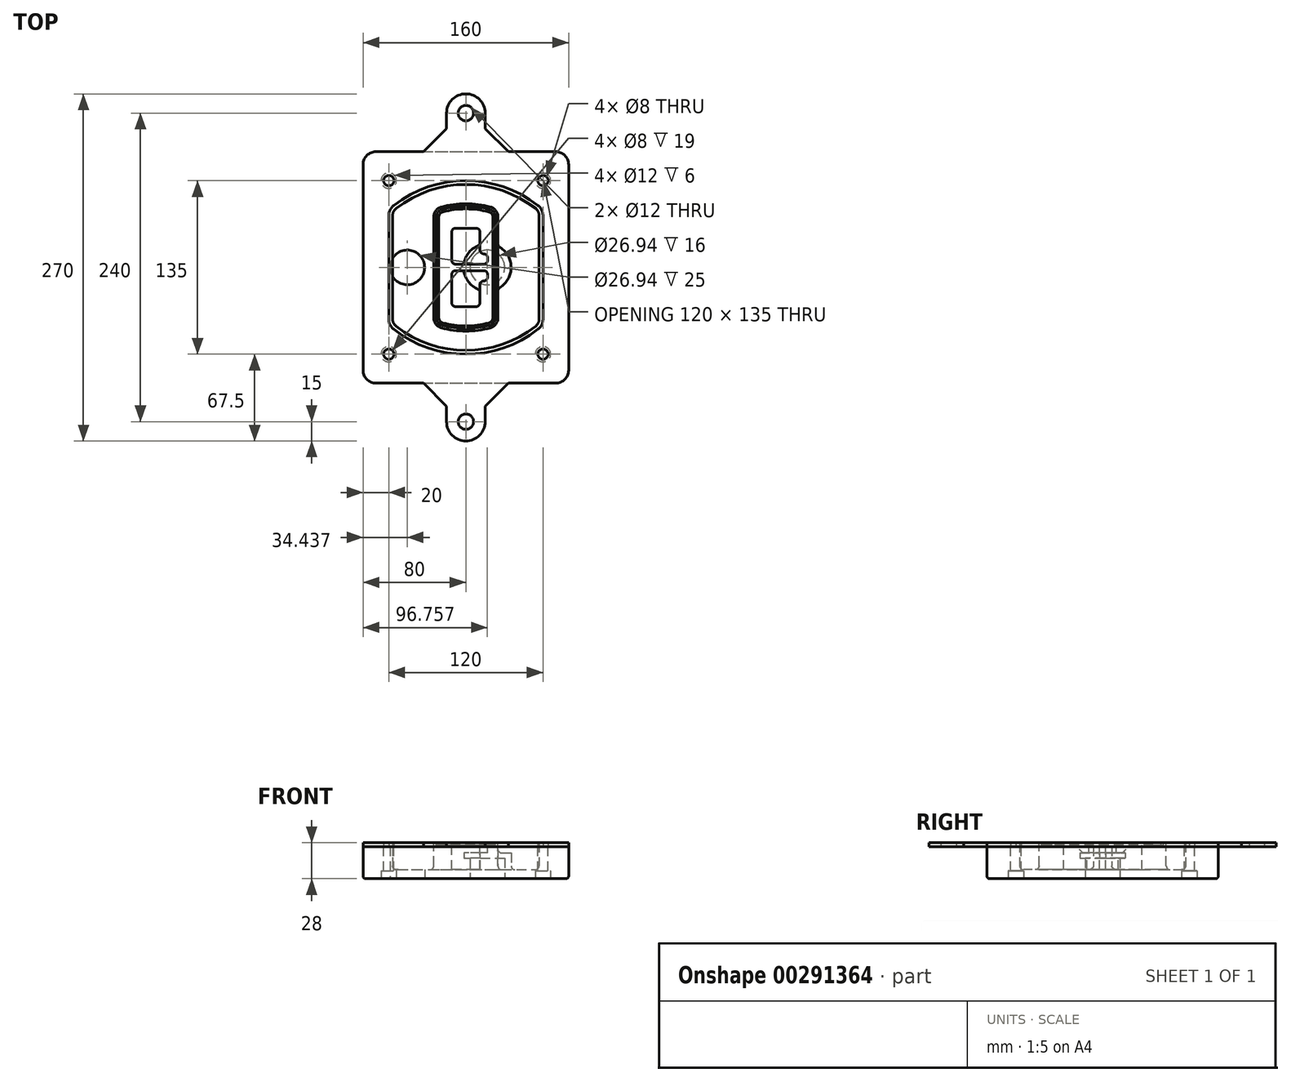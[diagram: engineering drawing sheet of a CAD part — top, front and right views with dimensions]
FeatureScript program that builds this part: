
annotation { "Feature Type Name" : "Feature", "Feature Type Description" : "" }
export const myFeature = defineFeature(function(context is Context, id is Id, definition is map)
    precondition{}
    {
        {
            var Q0;
            Q0=qCreatedBy(makeId("Top.planeOp"),FACE);
            var sketch = newSketch(context, id + "F0", { "sketchPlane" : qUnion([Q0])});
            skPoint(sketch, "E0.rect.middle", {"position": v(0, 0) * mm});
            skLineSegment(sketch, "E1.bottom", {"start": v(-70, -90) * mm, "end": v(70, -90) * mm});
            skLineSegment(sketch, "E1.top", {"start": v(-70, 90) * mm, "end": v(70, 90) * mm});
            skLineSegment(sketch, "E1.left", {"start": v(-80, -80) * mm, "end": v(-80, 80) * mm});
            skLineSegment(sketch, "E1.right", {"start": v(80, -80) * mm, "end": v(80, 80) * mm});
            skLineSegment(sketch, "E2", {"start": v(-80, 90) * mm, "end": v(80, -90) * mm, "construction": true});
            skLineSegment(sketch, "E3", {"start": v(80, 90) * mm, "end": v(-80, -90) * mm, "construction": true});
            skCircle(sketch, "E4", {"center": v(-60, 67.5) * mm, "radius": 4 * mm});
            skCircle(sketch, "E5", {"center": v(60, 67.5) * mm, "radius": 4 * mm});
            skCircle(sketch, "E6", {"center": v(60, -67.5) * mm, "radius": 4 * mm});
            skCircle(sketch, "E7", {"center": v(-60, -67.5) * mm, "radius": 4 * mm});
            skLineSegment(sketch, "E8", {"start": v(-60, 67.5) * mm, "end": v(60, 67.5) * mm, "construction": true});
            skLineSegment(sketch, "E9", {"start": v(60, 67.5) * mm, "end": v(60, -67.5) * mm, "construction": true});
            skLineSegment(sketch, "E10", {"start": v(60, -67.5) * mm, "end": v(-60, -67.5) * mm, "construction": true});
            skLineSegment(sketch, "E11", {"start": v(-60, -67.5) * mm, "end": v(-60, 67.5) * mm, "construction": true});
            skLineSegment(sketch, "E12", {"start": v(-60, 40.3) * mm, "end": v(-60, -40.3) * mm});
            skLineSegment(sketch, "E13", {"start": v(60, 40.3) * mm, "end": v(60, -40.3) * mm});
            skArc(sketch, "E14", {"start": v(56.15, 48.18) * mm, "mid": v(0, 67.5) * mm, "end": v(-56.15, 48.18) * mm});
            skArc(sketch, "E15", {"start": v(-56.15, -48.18) * mm, "mid": v(0, -67.5) * mm, "end": v(56.15, -48.18) * mm});
            skLineSegment(sketch, "E16", {"start": v(-60, 0) * mm, "end": v(60, 0) * mm, "construction": true});
            skPoint(sketch, "E17.visualSharp", {"position": v(-60, -45) * mm});
            skArc(sketch, "E17.filletArc", {"start": v(-60, -40.3) * mm, "mid": v(-58.99, -44.68) * mm, "end": v(-56.15, -48.18) * mm});
            skPoint(sketch, "E18.visualSharp", {"position": v(-60, 45) * mm});
            skArc(sketch, "E18.filletArc", {"start": v(-56.15, 48.18) * mm, "mid": v(-58.99, 44.68) * mm, "end": v(-60, 40.3) * mm});
            skPoint(sketch, "E19.visualSharp", {"position": v(60, 45) * mm});
            skArc(sketch, "E19.filletArc", {"start": v(60, 40.3) * mm, "mid": v(58.99, 44.68) * mm, "end": v(56.15, 48.18) * mm});
            skPoint(sketch, "E20.visualSharp", {"position": v(60, -45) * mm});
            skArc(sketch, "E20.filletArc", {"start": v(56.15, -48.18) * mm, "mid": v(58.99, -44.68) * mm, "end": v(60, -40.3) * mm});
            skPoint(sketch, "E21.visualSharp", {"position": v(-80, 90) * mm});
            skArc(sketch, "E21.filletArc", {"start": v(-70, 90) * mm, "mid": v(-77.07, 87.07) * mm, "end": v(-80, 80) * mm});
            skPoint(sketch, "E22.visualSharp", {"position": v(80, 90) * mm});
            skArc(sketch, "E22.filletArc", {"start": v(80, 80) * mm, "mid": v(77.07, 87.07) * mm, "end": v(70, 90) * mm});
            skPoint(sketch, "E23.visualSharp", {"position": v(80, -90) * mm});
            skArc(sketch, "E23.filletArc", {"start": v(70, -90) * mm, "mid": v(77.07, -87.07) * mm, "end": v(80, -80) * mm});
            skPoint(sketch, "E24.visualSharp", {"position": v(-80, -90) * mm});
            skArc(sketch, "E24.filletArc", {"start": v(-80, -80) * mm, "mid": v(-77.07, -87.07) * mm, "end": v(-70, -90) * mm});
            skArc(sketch, "E25.0", {"start": v(57, 40.3) * mm, "mid": v(56.3, 43.36) * mm, "end": v(54.3, 45.81) * mm});
            skLineSegment(sketch, "E25.1", {"start": v(57, 40.3) * mm, "end": v(57, -40.3) * mm});
            skArc(sketch, "E25.2", {"start": v(54.3, -45.81) * mm, "mid": v(56.3, -43.36) * mm, "end": v(57, -40.3) * mm});
            skArc(sketch, "E25.3", {"start": v(-54.3, -45.81) * mm, "mid": v(0, -64.5) * mm, "end": v(54.3, -45.81) * mm});
            skArc(sketch, "E25.4", {"start": v(-57, -40.3) * mm, "mid": v(-56.3, -43.36) * mm, "end": v(-54.3, -45.81) * mm});
            skArc(sketch, "E25.5", {"start": v(54.3, 45.81) * mm, "mid": v(0, 64.5) * mm, "end": v(-54.3, 45.81) * mm});
            skLineSegment(sketch, "E25.6", {"start": v(-57, 40.3) * mm, "end": v(-57, -40.3) * mm});
            skArc(sketch, "E25.7", {"start": v(-54.3, 45.81) * mm, "mid": v(-56.3, 43.36) * mm, "end": v(-57, 40.3) * mm});
            skArc(sketch, "E26.0", {"start": v(-58.62, 51.33) * mm, "mid": v(-62.58, 46.43) * mm, "end": v(-64, 40.3) * mm});
            skArc(sketch, "E26.1", {"start": v(58.62, 51.33) * mm, "mid": v(0, 71.5) * mm, "end": v(-58.62, 51.33) * mm});
            skArc(sketch, "E26.2", {"start": v(64, 40.3) * mm, "mid": v(62.58, 46.43) * mm, "end": v(58.62, 51.33) * mm});
            skLineSegment(sketch, "E26.3", {"start": v(64, 40.3) * mm, "end": v(64, -40.3) * mm});
            skArc(sketch, "E26.4", {"start": v(58.62, -51.33) * mm, "mid": v(62.58, -46.43) * mm, "end": v(64, -40.3) * mm});
            skLineSegment(sketch, "E26.5", {"start": v(-64, 40.3) * mm, "end": v(-64, -40.3) * mm});
            skArc(sketch, "E26.6", {"start": v(-58.62, -51.33) * mm, "mid": v(0, -71.5) * mm, "end": v(58.62, -51.33) * mm});
            skArc(sketch, "E26.7", {"start": v(-64, -40.3) * mm, "mid": v(-62.58, -46.43) * mm, "end": v(-58.62, -51.33) * mm});
            skSolve(sketch);
        }
        {
            var Q0;
            Q0=makeQuery(id+"F0.imprint","IMPRINT",FACE,{"disambiguationData":[TD([[makeQuery(id+"F0.imprint","IMPRINT",EDGE,{"derivedFrom":sQuery(id+"F0.wireOp",EDGE,"E1.bottom")}),1.0]])]});
            var Q1;
            Q1=makeQuery(id+"F0.imprint","IMPRINT",FACE,{"disambiguationData":[TD([[makeQuery(id+"F0.imprint","IMPRINT",EDGE,{"derivedFrom":sQuery(id+"F0.wireOp",EDGE,"E12")}),1.0]])]});
            var Q2;
            Q2=makeQuery(id+"F0.imprint","IMPRINT",FACE,{"disambiguationData":[TD([[makeQuery(id+"F0.imprint","IMPRINT",EDGE,{"derivedFrom":sQuery(id+"F0.wireOp",EDGE,"E25.0")}),1.0]])]});
            var Q3;
            Q3=makeQuery(id+"F0.imprint","IMPRINT",FACE,{"disambiguationData":[TD([[makeQuery(id+"F0.imprint","IMPRINT",EDGE,{"derivedFrom":sQuery(id+"F0.wireOp",EDGE,"E12")}),-1.0]])]});
            extrude(context, id + "F1", {"entities" : qUnion([Q0, Q1, Q2, Q3]), "oppositeDirection" : true, "depth" : 25 * mm});
        }
        {
            var Q0;
            Q0=makeQuery(id+"F0.imprint","IMPRINT",FACE,{"disambiguationData":[TD([[makeQuery(id+"F0.imprint","IMPRINT",EDGE,{"derivedFrom":sQuery(id+"F0.wireOp",EDGE,"E12")}),1.0]])]});
            extrude(context, id + "F2", {"entities" : qUnion([Q0]), "operationType" : NewBodyOperationType.ADD, "depth" : 3 * mm});
        }
        {
            var Q0;
            Q0=makeQuery(id+"F0.imprint","IMPRINT",FACE,{"disambiguationData":[TD([[makeQuery(id+"F0.imprint","IMPRINT",EDGE,{"derivedFrom":sQuery(id+"F0.wireOp",EDGE,"E25.0")}),1.0]])]});
            extrude(context, id + "F3", {"entities" : qUnion([Q0]), "operationType" : NewBodyOperationType.REMOVE, "oppositeDirection" : true, "depth" : 18 * mm});
        }
        {
            var Q0;
            Q0=makeQuery(id+"F2.opExtrude","CAP_FACE",FACE,{"disambiguationData":[OSD([sQuery(id+"F0.wireOp",EDGE,"E12"),sQuery(id+"F0.wireOp",EDGE,"E13"),sQuery(id+"F0.wireOp",EDGE,"E14"),sQuery(id+"F0.wireOp",EDGE,"E15"),sQuery(id+"F0.wireOp",EDGE,"E17.filletArc"),sQuery(id+"F0.wireOp",EDGE,"E18.filletArc"),sQuery(id+"F0.wireOp",EDGE,"E19.filletArc"),sQuery(id+"F0.wireOp",EDGE,"E20.filletArc"),sQuery(id+"F0.wireOp",EDGE,"E25.0"),sQuery(id+"F0.wireOp",EDGE,"E25.1"),sQuery(id+"F0.wireOp",EDGE,"E25.2"),sQuery(id+"F0.wireOp",EDGE,"E25.3"),sQuery(id+"F0.wireOp",EDGE,"E25.4"),sQuery(id+"F0.wireOp",EDGE,"E25.5"),sQuery(id+"F0.wireOp",EDGE,"E25.6"),sQuery(id+"F0.wireOp",EDGE,"E25.7")])],"isStart":false});
            var sketch = newSketch(context, id + "F4", { "sketchPlane" : qUnion([Q0])});
            skArc(sketch, "E27.0", {"start": v(-19.08, -46.97) * mm, "mid": v(0, -49.5) * mm, "end": v(19.08, -46.97) * mm});
            skArc(sketch, "E28.0", {"start": v(19.08, 46.97) * mm, "mid": v(0, 49.5) * mm, "end": v(-19.08, 46.97) * mm});
            skLineSegment(sketch, "E29", {"start": v(-25, 39.25) * mm, "end": v(-25, -39.25) * mm});
            skLineSegment(sketch, "E30", {"start": v(25, 39.25) * mm, "end": v(25, -39.25) * mm});
            skLineSegment(sketch, "E31", {"start": v(-25, 45.1) * mm, "end": v(25, 45.1) * mm, "construction": true});
            skLineSegment(sketch, "E32", {"start": v(-25, -45.1) * mm, "end": v(25, -45.1) * mm, "construction": true});
            skPoint(sketch, "E33.visualSharp", {"position": v(-25, 45.1) * mm});
            skArc(sketch, "E33.filletArc", {"start": v(-19.08, 46.97) * mm, "mid": v(-23.35, 44.11) * mm, "end": v(-25, 39.25) * mm});
            skPoint(sketch, "E34.visualSharp", {"position": v(25, 45.1) * mm});
            skArc(sketch, "E34.filletArc", {"start": v(25, 39.25) * mm, "mid": v(23.35, 44.11) * mm, "end": v(19.08, 46.97) * mm});
            skPoint(sketch, "E35.visualSharp", {"position": v(25, -45.1) * mm});
            skArc(sketch, "E35.filletArc", {"start": v(19.08, -46.97) * mm, "mid": v(23.35, -44.11) * mm, "end": v(25, -39.25) * mm});
            skPoint(sketch, "E36.visualSharp", {"position": v(-25, -45.1) * mm});
            skArc(sketch, "E36.filletArc", {"start": v(-25, -39.25) * mm, "mid": v(-23.35, -44.11) * mm, "end": v(-19.08, -46.97) * mm});
            skArc(sketch, "E37.0", {"start": v(54.3, 45.81) * mm, "mid": v(0, 64.5) * mm, "end": v(-54.3, 45.81) * mm});
            skArc(sketch, "E37.1", {"start": v(-54.3, 45.81) * mm, "mid": v(-56.3, 43.36) * mm, "end": v(-57, 40.3) * mm});
            skLineSegment(sketch, "E37.2", {"start": v(-57, 40.3) * mm, "end": v(-57, -40.3) * mm});
            skArc(sketch, "E37.3", {"start": v(-57, -40.3) * mm, "mid": v(-56.3, -43.36) * mm, "end": v(-54.3, -45.81) * mm});
            skArc(sketch, "E37.4", {"start": v(-54.3, -45.81) * mm, "mid": v(0, -64.5) * mm, "end": v(54.3, -45.81) * mm});
            skArc(sketch, "E37.5", {"start": v(54.3, -45.81) * mm, "mid": v(56.3, -43.36) * mm, "end": v(57, -40.3) * mm});
            skLineSegment(sketch, "E37.6", {"start": v(57, 40.3) * mm, "end": v(57, -40.3) * mm});
            skArc(sketch, "E37.7", {"start": v(57, 40.3) * mm, "mid": v(56.3, 43.36) * mm, "end": v(54.3, 45.81) * mm});
            skLineSegment(sketch, "E38.0", {"start": v(23, 39.25) * mm, "end": v(23, -39.25) * mm});
            skArc(sketch, "E38.1", {"start": v(18.56, -45.04) * mm, "mid": v(21.76, -42.9) * mm, "end": v(23, -39.25) * mm});
            skArc(sketch, "E38.2", {"start": v(-18.56, -45.04) * mm, "mid": v(0, -47.5) * mm, "end": v(18.56, -45.04) * mm});
            skArc(sketch, "E38.3", {"start": v(-23, -39.25) * mm, "mid": v(-21.76, -42.9) * mm, "end": v(-18.56, -45.04) * mm});
            skLineSegment(sketch, "E38.4", {"start": v(-23, 39.25) * mm, "end": v(-23, -39.25) * mm});
            skArc(sketch, "E38.5", {"start": v(23, 39.25) * mm, "mid": v(21.76, 42.9) * mm, "end": v(18.56, 45.04) * mm});
            skArc(sketch, "E38.6", {"start": v(-18.56, 45.04) * mm, "mid": v(-21.76, 42.9) * mm, "end": v(-23, 39.25) * mm});
            skArc(sketch, "E38.7", {"start": v(18.56, 45.04) * mm, "mid": v(0, 47.5) * mm, "end": v(-18.56, 45.04) * mm});
            skArc(sketch, "E39.0", {"start": v(21, 39.25) * mm, "mid": v(20.18, 41.68) * mm, "end": v(18.04, 43.1) * mm});
            skLineSegment(sketch, "E39.1", {"start": v(21, 39.25) * mm, "end": v(21, -39.25) * mm});
            skArc(sketch, "E39.2", {"start": v(18.04, -43.1) * mm, "mid": v(20.18, -41.68) * mm, "end": v(21, -39.25) * mm});
            skArc(sketch, "E39.3", {"start": v(-18.04, -43.1) * mm, "mid": v(0, -45.5) * mm, "end": v(18.04, -43.1) * mm});
            skArc(sketch, "E39.4", {"start": v(-21, -39.25) * mm, "mid": v(-20.18, -41.68) * mm, "end": v(-18.04, -43.1) * mm});
            skArc(sketch, "E39.5", {"start": v(18.04, 43.1) * mm, "mid": v(0, 45.5) * mm, "end": v(-18.04, 43.1) * mm});
            skLineSegment(sketch, "E39.6", {"start": v(-21, 39.25) * mm, "end": v(-21, -39.25) * mm});
            skArc(sketch, "E39.7", {"start": v(-18.04, 43.1) * mm, "mid": v(-20.18, 41.68) * mm, "end": v(-21, 39.25) * mm});
            skLineSegment(sketch, "E40", {"start": v(-25, 0) * mm, "end": v(25, 0) * mm, "construction": true});
            skLineSegment(sketch, "E41", {"start": v(-11, 5.5) * mm, "end": v(-11, 27.5) * mm});
            skLineSegment(sketch, "E42", {"start": v(-8, 30.5) * mm, "end": v(8, 30.5) * mm});
            skLineSegment(sketch, "E43", {"start": v(11, 27.5) * mm, "end": v(11, 13.5) * mm});
            skLineSegment(sketch, "E44", {"start": v(14, 10.5) * mm, "end": v(14, 10.5) * mm});
            skLineSegment(sketch, "E45", {"start": v(17, 7.5) * mm, "end": v(17, 5.5) * mm});
            skLineSegment(sketch, "E46", {"start": v(14, 2.5) * mm, "end": v(-8, 2.5) * mm});
            skPoint(sketch, "E47.visualSharp", {"position": v(-11, 30.5) * mm});
            skArc(sketch, "E47.filletArc", {"start": v(-8, 30.5) * mm, "mid": v(-10.12, 29.62) * mm, "end": v(-11, 27.5) * mm});
            skPoint(sketch, "E48.visualSharp", {"position": v(11, 30.5) * mm});
            skArc(sketch, "E48.filletArc", {"start": v(11, 27.5) * mm, "mid": v(10.12, 29.62) * mm, "end": v(8, 30.5) * mm});
            skPoint(sketch, "E49.visualSharp", {"position": v(11, 10.5) * mm});
            skArc(sketch, "E49.filletArc", {"start": v(11, 13.5) * mm, "mid": v(11.88, 11.38) * mm, "end": v(14, 10.5) * mm});
            skPoint(sketch, "E50.visualSharp", {"position": v(17, 10.5) * mm});
            skArc(sketch, "E50.filletArc", {"start": v(17, 7.5) * mm, "mid": v(16.12, 9.62) * mm, "end": v(14, 10.5) * mm});
            skPoint(sketch, "E51.visualSharp", {"position": v(17, 2.5) * mm});
            skArc(sketch, "E51.filletArc", {"start": v(14, 2.5) * mm, "mid": v(16.12, 3.38) * mm, "end": v(17, 5.5) * mm});
            skPoint(sketch, "E52.visualSharp", {"position": v(-11, 2.5) * mm});
            skArc(sketch, "E52.filletArc", {"start": v(-11, 5.5) * mm, "mid": v(-10.12, 3.38) * mm, "end": v(-8, 2.5) * mm});
            skLineSegment(sketch, "E53.0.MirrorCS", {"start": v(14, -2.5) * mm, "end": v(-8, -2.5) * mm});
            skArc(sketch, "E54.0.MirrorCS", {"start": v(-11, -5.5) * mm, "mid": v(-10.12, -3.38) * mm, "end": v(-8, -2.5) * mm});
            skLineSegment(sketch, "E55.0.MirrorCS", {"start": v(-11, -5.5) * mm, "end": v(-11, -27.5) * mm});
            skArc(sketch, "E56.0.MirrorCS", {"start": v(-8, -30.5) * mm, "mid": v(-10.12, -29.62) * mm, "end": v(-11, -27.5) * mm});
            skLineSegment(sketch, "E57.0.MirrorCS", {"start": v(-8, -30.5) * mm, "end": v(8, -30.5) * mm});
            skArc(sketch, "E58.0.MirrorCS", {"start": v(11, -27.5) * mm, "mid": v(10.12, -29.62) * mm, "end": v(8, -30.5) * mm});
            skLineSegment(sketch, "E59.0.MirrorCS", {"start": v(11, -27.5) * mm, "end": v(11, -13.5) * mm});
            skArc(sketch, "E60.0.MirrorCS", {"start": v(11, -13.5) * mm, "mid": v(11.88, -11.38) * mm, "end": v(14, -10.5) * mm});
            skArc(sketch, "E61.0.MirrorCS", {"start": v(17, -7.5) * mm, "mid": v(16.12, -9.62) * mm, "end": v(14, -10.5) * mm});
            skLineSegment(sketch, "E62.0.MirrorCS", {"start": v(17, -7.5) * mm, "end": v(17, -5.5) * mm});
            skArc(sketch, "E63.0.MirrorCS", {"start": v(14, -2.5) * mm, "mid": v(16.12, -3.38) * mm, "end": v(17, -5.5) * mm});
            skSolve(sketch);
        }
        {
            var Q0;
            Q0=makeQuery(id+"F4.imprint","IMPRINT",FACE,{"disambiguationData":[TD([[makeQuery(id+"F4.imprint","IMPRINT",EDGE,{"derivedFrom":sQuery(id+"F4.wireOp",EDGE,"E27.0")}),1.0]])]});
            var Q1;
            Q1=makeQuery(id+"F4.imprint","IMPRINT",FACE,{"disambiguationData":[TD([[makeQuery(id+"F4.imprint","IMPRINT",EDGE,{"derivedFrom":sQuery(id+"F4.wireOp",EDGE,"E38.0")}),-1.0]])]});
            var Q2;
            Q2=makeQuery(id+"F4.imprint","IMPRINT",FACE,{"disambiguationData":[TD([[makeQuery(id+"F4.imprint","IMPRINT",EDGE,{"derivedFrom":sQuery(id+"F4.wireOp",EDGE,"E39.0")}),1.0]])]});
            extrude(context, id + "F5", {"entities" : qUnion([Q0, Q1, Q2]), "operationType" : NewBodyOperationType.ADD, "endBound" : BoundingType.UP_TO_NEXT, "oppositeDirection" : true, "depth" : 25 * mm});
        }
        {
            var Q0;
            Q0=makeQuery(id+"F4.imprint","IMPRINT",FACE,{"disambiguationData":[TD([[makeQuery(id+"F4.imprint","IMPRINT",EDGE,{"derivedFrom":sQuery(id+"F4.wireOp",EDGE,"E38.0")}),-1.0]])]});
            extrude(context, id + "F6", {"entities" : qUnion([Q0]), "operationType" : NewBodyOperationType.REMOVE, "oppositeDirection" : true, "depth" : 2 * mm});
        }
        {
            var Q0;
            Q0=makeQuery(id+"F1.opExtrude","CAP_FACE",FACE,{"disambiguationData":[OSD([sQuery(id+"F0.wireOp",EDGE,"E1.bottom"),sQuery(id+"F0.wireOp",EDGE,"E1.top"),sQuery(id+"F0.wireOp",EDGE,"E1.left"),sQuery(id+"F0.wireOp",EDGE,"E1.right"),sQuery(id+"F0.wireOp",EDGE,"E4"),sQuery(id+"F0.wireOp",EDGE,"E5"),sQuery(id+"F0.wireOp",EDGE,"E6"),sQuery(id+"F0.wireOp",EDGE,"E7"),sQuery(id+"F0.wireOp",EDGE,"E21.filletArc"),sQuery(id+"F0.wireOp",EDGE,"E22.filletArc"),sQuery(id+"F0.wireOp",EDGE,"E23.filletArc"),sQuery(id+"F0.wireOp",EDGE,"E24.filletArc")])],"isStart":false});
            var sketch = newSketch(context, id + "F7", { "sketchPlane" : qUnion([Q0])});
            skCircle(sketch, "E64", {"center": v(16.76, 0) * mm, "radius": 13.47 * mm});
            skCircle(sketch, "E65", {"center": v(-45.56, 0) * mm, "radius": 13.47 * mm});
            skLineSegment(sketch, "E66", {"start": v(80, 0) * mm, "end": v(-80, 0) * mm});
            skCircle(sketch, "E67", {"center": v(16.76, 0) * mm, "radius": 18.47 * mm});
            skCircle(sketch, "E68", {"center": v(60, -67.5) * mm, "radius": 6 * mm});
            skCircle(sketch, "E69", {"center": v(-60, -67.5) * mm, "radius": 6 * mm});
            skCircle(sketch, "E70", {"center": v(-60, 67.5) * mm, "radius": 6 * mm});
            skCircle(sketch, "E71", {"center": v(60, 67.5) * mm, "radius": 6 * mm});
            skSolve(sketch);
        }
        {
            var Q0;
            {var subQ1=sQuery(id+"F7.wireOp",EDGE,"E66");var subQ4=sQuery(id+"F7.wireOp",EDGE,"E64");var subQ6=makeQuery(id+"F7.imprint","INTERSECT",VERTEX,{"disambiguationData":[OD(0.0)],"derivedFrom":[subQ4,subQ1]});Q0=makeQuery(id+"F7.imprint","IMPRINT",FACE,{"disambiguationData":[TD([[makeQuery(id+"F7.imprint","IMPRINT",EDGE,{"disambiguationData":[TD([[subQ6,-1.0]])],"derivedFrom":subQ4}),-1.0]])]});}
            var Q1;
            {var subQ0=sQuery(id+"F7.wireOp",EDGE,"E66");var subQ1=sQuery(id+"F7.wireOp",EDGE,"E64");var subQ3=makeQuery(id+"F7.imprint","INTERSECT",VERTEX,{"disambiguationData":[OD(0.0)],"derivedFrom":[subQ1,subQ0]});Q1=makeQuery(id+"F7.imprint","IMPRINT",FACE,{"disambiguationData":[TD([[makeQuery(id+"F7.imprint","IMPRINT",EDGE,{"disambiguationData":[TD([[subQ3,-1.0]])],"derivedFrom":subQ1}),1.0]])]});}
            var Q2;
            {var subQ0=sQuery(id+"F7.wireOp",EDGE,"E66");var subQ1=sQuery(id+"F7.wireOp",EDGE,"E64");var subQ3=makeQuery(id+"F7.imprint","INTERSECT",VERTEX,{"disambiguationData":[OD(0.0)],"derivedFrom":[subQ1,subQ0]});Q2=makeQuery(id+"F7.imprint","IMPRINT",FACE,{"disambiguationData":[TD([[makeQuery(id+"F7.imprint","IMPRINT",EDGE,{"disambiguationData":[TD([[subQ3,1.0]])],"derivedFrom":subQ1}),1.0]])]});}
            var Q3;
            {var subQ1=sQuery(id+"F7.wireOp",EDGE,"E66");var subQ4=sQuery(id+"F7.wireOp",EDGE,"E64");var subQ6=makeQuery(id+"F7.imprint","INTERSECT",VERTEX,{"disambiguationData":[OD(0.0)],"derivedFrom":[subQ4,subQ1]});Q3=makeQuery(id+"F7.imprint","IMPRINT",FACE,{"disambiguationData":[TD([[makeQuery(id+"F7.imprint","IMPRINT",EDGE,{"disambiguationData":[TD([[subQ6,1.0]])],"derivedFrom":subQ4}),-1.0]])]});}
            extrude(context, id + "F8", {"entities" : qUnion([Q0, Q1, Q2, Q3]), "operationType" : NewBodyOperationType.ADD, "oppositeDirection" : true, "depth" : 20 * mm});
        }
        {
            var Q0;
            {var subQ0=sQuery(id+"F7.wireOp",EDGE,"E66");var subQ1=sQuery(id+"F7.wireOp",EDGE,"E64");var subQ3=makeQuery(id+"F7.imprint","INTERSECT",VERTEX,{"disambiguationData":[OD(0.0)],"derivedFrom":[subQ1,subQ0]});Q0=makeQuery(id+"F7.imprint","IMPRINT",FACE,{"disambiguationData":[TD([[makeQuery(id+"F7.imprint","IMPRINT",EDGE,{"disambiguationData":[TD([[subQ3,-1.0]])],"derivedFrom":subQ1}),1.0]])]});}
            var Q1;
            {var subQ0=sQuery(id+"F7.wireOp",EDGE,"E66");var subQ1=sQuery(id+"F7.wireOp",EDGE,"E64");var subQ3=makeQuery(id+"F7.imprint","INTERSECT",VERTEX,{"disambiguationData":[OD(0.0)],"derivedFrom":[subQ1,subQ0]});Q1=makeQuery(id+"F7.imprint","IMPRINT",FACE,{"disambiguationData":[TD([[makeQuery(id+"F7.imprint","IMPRINT",EDGE,{"disambiguationData":[TD([[subQ3,1.0]])],"derivedFrom":subQ1}),1.0]])]});}
            extrude(context, id + "F9", {"entities" : qUnion([Q0, Q1]), "operationType" : NewBodyOperationType.REMOVE, "oppositeDirection" : true, "depth" : 16 * mm});
        }
        {
            var Q0;
            {var subQ0=sQuery(id+"F7.wireOp",EDGE,"E66");var subQ1=sQuery(id+"F7.wireOp",EDGE,"E65");var subQ3=makeQuery(id+"F7.imprint","INTERSECT",VERTEX,{"disambiguationData":[OD(0.0)],"derivedFrom":[subQ1,subQ0]});Q0=makeQuery(id+"F7.imprint","IMPRINT",FACE,{"disambiguationData":[TD([[makeQuery(id+"F7.imprint","IMPRINT",EDGE,{"disambiguationData":[TD([[subQ3,-1.0]])],"derivedFrom":subQ1}),1.0]])]});}
            var Q1;
            {var subQ0=sQuery(id+"F7.wireOp",EDGE,"E66");var subQ1=sQuery(id+"F7.wireOp",EDGE,"E65");var subQ3=makeQuery(id+"F7.imprint","INTERSECT",VERTEX,{"disambiguationData":[OD(0.0)],"derivedFrom":[subQ1,subQ0]});Q1=makeQuery(id+"F7.imprint","IMPRINT",FACE,{"disambiguationData":[TD([[makeQuery(id+"F7.imprint","IMPRINT",EDGE,{"disambiguationData":[TD([[subQ3,1.0]])],"derivedFrom":subQ1}),1.0]])]});}
            extrude(context, id + "F10", {"entities" : qUnion([Q0, Q1]), "operationType" : NewBodyOperationType.REMOVE, "oppositeDirection" : true, "depth" : 25 * mm});
        }
        {
            var Q0;
            Q0=makeQuery(id+"F7.imprint","IMPRINT",FACE,{"disambiguationData":[TD([[makeQuery(id+"F7.imprint","IMPRINT",EDGE,{"derivedFrom":sQuery(id+"F7.wireOp",EDGE,"E68")}),1.0]])]});
            var Q1;
            Q1=makeQuery(id+"F7.imprint","IMPRINT",FACE,{"disambiguationData":[TD([[makeQuery(id+"F7.imprint","IMPRINT",EDGE,{"derivedFrom":makeQuery(id+"F1.opExtrude","CAP_EDGE",EDGE,{"disambiguationData":[OSD([sQuery(id+"F0.wireOp",EDGE,"E5")])],"isStart":false})}),-1.0]])]});
            var Q2;
            Q2=makeQuery(id+"F7.imprint","IMPRINT",FACE,{"disambiguationData":[TD([[makeQuery(id+"F7.imprint","IMPRINT",EDGE,{"derivedFrom":sQuery(id+"F7.wireOp",EDGE,"E69")}),1.0]])]});
            var Q3;
            Q3=makeQuery(id+"F7.imprint","IMPRINT",FACE,{"disambiguationData":[TD([[makeQuery(id+"F7.imprint","IMPRINT",EDGE,{"derivedFrom":makeQuery(id+"F1.opExtrude","CAP_EDGE",EDGE,{"disambiguationData":[OSD([sQuery(id+"F0.wireOp",EDGE,"E4")])],"isStart":false})}),-1.0]])]});
            var Q4;
            Q4=makeQuery(id+"F7.imprint","IMPRINT",FACE,{"disambiguationData":[TD([[makeQuery(id+"F7.imprint","IMPRINT",EDGE,{"derivedFrom":sQuery(id+"F7.wireOp",EDGE,"E70")}),1.0]])]});
            var Q5;
            Q5=makeQuery(id+"F7.imprint","IMPRINT",FACE,{"disambiguationData":[TD([[makeQuery(id+"F7.imprint","IMPRINT",EDGE,{"derivedFrom":makeQuery(id+"F1.opExtrude","CAP_EDGE",EDGE,{"disambiguationData":[OSD([sQuery(id+"F0.wireOp",EDGE,"E7")])],"isStart":false})}),-1.0]])]});
            var Q6;
            Q6=makeQuery(id+"F7.imprint","IMPRINT",FACE,{"disambiguationData":[TD([[makeQuery(id+"F7.imprint","IMPRINT",EDGE,{"derivedFrom":sQuery(id+"F7.wireOp",EDGE,"E71")}),1.0]])]});
            var Q7;
            Q7=makeQuery(id+"F7.imprint","IMPRINT",FACE,{"disambiguationData":[TD([[makeQuery(id+"F7.imprint","IMPRINT",EDGE,{"derivedFrom":makeQuery(id+"F1.opExtrude","CAP_EDGE",EDGE,{"disambiguationData":[OSD([sQuery(id+"F0.wireOp",EDGE,"E6")])],"isStart":false})}),-1.0]])]});
            extrude(context, id + "F11", {"entities" : qUnion([Q0, Q1, Q2, Q3, Q4, Q5, Q6, Q7]), "operationType" : NewBodyOperationType.REMOVE, "oppositeDirection" : true, "depth" : 6 * mm});
        }
        {
            var Q0;
            Q0=makeQuery(id+"F9.boolean.opBoolean","COPY",FACE,{"derivedFrom":makeQuery(id+"F9.opExtrude","CAP_FACE",FACE,{"disambiguationData":[OSD([sQuery(id+"F7.wireOp",EDGE,"E64")])],"isStart":false})});
            var sketch = newSketch(context, id + "F12", { "sketchPlane" : qUnion([Q0])});
            skArc(sketch, "E72.0", {"start": v(11, 17.55) * mm, "mid": v(2.57, 11.82) * mm, "end": v(-1.54, 2.5) * mm});
            skArc(sketch, "E72.1", {"start": v(-1.54, -2.5) * mm, "mid": v(2.57, -11.82) * mm, "end": v(11, -17.55) * mm});
            skLineSegment(sketch, "E73", {"start": v(-1.54, -2.5) * mm, "end": v(14, -2.5) * mm});
            skLineSegment(sketch, "E74.0", {"start": v(14, 2.5) * mm, "end": v(-1.54, 2.5) * mm});
            skArc(sketch, "E74.1", {"start": v(14, 2.5) * mm, "mid": v(16.12, 3.38) * mm, "end": v(17, 5.5) * mm});
            skLineSegment(sketch, "E74.2", {"start": v(17, 7.5) * mm, "end": v(17, 5.5) * mm});
            skArc(sketch, "E74.3", {"start": v(17, 7.5) * mm, "mid": v(16.12, 9.62) * mm, "end": v(14, 10.5) * mm});
            skArc(sketch, "E74.4", {"start": v(11, 13.5) * mm, "mid": v(11.88, 11.38) * mm, "end": v(14, 10.5) * mm});
            skLineSegment(sketch, "E74.5", {"start": v(11, 17.55) * mm, "end": v(11, 13.5) * mm});
            skLineSegment(sketch, "E74.7", {"start": v(14, -2.5) * mm, "end": v(-1.54, -2.5) * mm});
            skArc(sketch, "E74.8", {"start": v(14, -2.5) * mm, "mid": v(16.12, -3.38) * mm, "end": v(17, -5.5) * mm});
            skLineSegment(sketch, "E74.9", {"start": v(17, -7.5) * mm, "end": v(17, -5.5) * mm});
            skArc(sketch, "E74.10", {"start": v(17, -7.5) * mm, "mid": v(16.12, -9.62) * mm, "end": v(14, -10.5) * mm});
            skArc(sketch, "E74.11", {"start": v(11, -13.5) * mm, "mid": v(11.88, -11.38) * mm, "end": v(14, -10.5) * mm});
            skLineSegment(sketch, "E74.12", {"start": v(11, -17.55) * mm, "end": v(11, -13.5) * mm});
            skPoint(sketch, "E75.orphan", {"position": v(11, -27.5) * mm});
            skPoint(sketch, "E76.orphan", {"position": v(-8, -2.5) * mm});
            skPoint(sketch, "E77.orphan", {"position": v(-8, 2.5) * mm});
            skPoint(sketch, "E78.orphan", {"position": v(11, 27.5) * mm});
            skSolve(sketch);
        }
        {
            var Q0;
            {var subQ7=sQuery(id+"F12.wireOp",EDGE,"E72.0");var subQ14=sQuery(id+"F12.wireOp",EDGE,"E72.1");var subQ16=sQuery(id+"F12.wireOp",EDGE,"E74.1");var subQ18=sQuery(id+"F12.wireOp",EDGE,"E74.8");Q0=qUnion([makeQuery(id+"F12.imprint","IMPRINT",FACE,{"disambiguationData":[TD([[makeQuery(id+"F12.imprint","IMPRINT",EDGE,{"derivedFrom":subQ7}),1.0]])]}),makeQuery(id+"F12.imprint","IMPRINT",FACE,{"disambiguationData":[TD([[makeQuery(id+"F12.imprint","IMPRINT",EDGE,{"derivedFrom":subQ14}),1.0]])]}),makeQuery(id+"F12.imprint","IMPRINT",FACE,{"disambiguationData":[TD([[makeQuery(id+"F12.imprint","IMPRINT",EDGE,{"derivedFrom":subQ16}),1.0]])]}),makeQuery(id+"F12.imprint","IMPRINT",FACE,{"disambiguationData":[TD([[makeQuery(id+"F12.imprint","IMPRINT",EDGE,{"derivedFrom":subQ18}),-1.0]])]})]);}
            var Q1;
            Q1=makeQuery(id+"F5.boolean.opBoolean","SPLIT",FACE,{"disambiguationData":[TD([makeQuery(id+"F5.opExtrude","SWEPT_FACE",FACE,{"disambiguationData":[OSD([sQuery(id+"F4.wireOp",EDGE,"E41")])]})])],"derivedFrom":makeQuery(id+"F3.boolean.opBoolean","COPY",FACE,{"derivedFrom":makeQuery(id+"F3.opExtrude","CAP_FACE",FACE,{"disambiguationData":[OSD([sQuery(id+"F0.wireOp",EDGE,"E25.0"),sQuery(id+"F0.wireOp",EDGE,"E25.1"),sQuery(id+"F0.wireOp",EDGE,"E25.2"),sQuery(id+"F0.wireOp",EDGE,"E25.3"),sQuery(id+"F0.wireOp",EDGE,"E25.4"),sQuery(id+"F0.wireOp",EDGE,"E25.5"),sQuery(id+"F0.wireOp",EDGE,"E25.6"),sQuery(id+"F0.wireOp",EDGE,"E25.7")])],"isStart":false})})});
            extrude(context, id + "F13", {"entities" : qUnion([Q0]), "operationType" : NewBodyOperationType.REMOVE, "endBound" : BoundingType.UP_TO_SURFACE, "endBoundEntityFace" : qUnion([Q1]), "depth" : 25 * mm});
        }
        {
            var Q0;
            Q0=makeQuery(id+"F3.boolean.opBoolean","COPY",EDGE,{"derivedFrom":makeQuery(id+"F3.opExtrude","CAP_EDGE",EDGE,{"disambiguationData":[OSD([sQuery(id+"F0.wireOp",EDGE,"E25.6")])],"isStart":false})});
            var Q1;
            Q1=makeQuery(id+"F8.boolean.opBoolean","INTERSECT",EDGE,{"derivedFrom":[makeQuery(id+"F5.opExtrude","SWEPT_FACE",FACE,{"disambiguationData":[OSD([sQuery(id+"F4.wireOp",EDGE,"E30")])]}),makeQuery(id+"F8.opExtrude","CAP_FACE",FACE,{"disambiguationData":[OSD([sQuery(id+"F7.wireOp",EDGE,"E67")])],"isStart":false})]});
            var Q2;
            Q2=makeQuery(id+"F8.boolean.opBoolean","INTERSECT",EDGE,{"disambiguationData":[OD(1.0)],"derivedFrom":[makeQuery(id+"F5.opExtrude","SWEPT_FACE",FACE,{"disambiguationData":[OSD([sQuery(id+"F4.wireOp",EDGE,"E30")])]}),makeQuery(id+"F8.opExtrude","SWEPT_FACE",FACE,{"disambiguationData":[OSD([sQuery(id+"F7.wireOp",EDGE,"E67")])]})]});
            var Q3;
            {var subQ0=sQuery(id+"F4.wireOp",EDGE,"E30");Q3=makeQuery(id+"F8.boolean.opBoolean","SPLIT",EDGE,{"disambiguationData":[TD([makeQuery(id+"F5.opExtrude","SWEPT_FACE",FACE,{"disambiguationData":[OSD([sQuery(id+"F4.wireOp",EDGE,"E35.filletArc")])]})])],"derivedFrom":makeQuery(id+"F5.opExtrude","CAP_EDGE",EDGE,{"disambiguationData":[OSD([subQ0])],"isStart":false})});}
            var Q4;
            {var subQ0=sQuery(id+"F0.wireOp",EDGE,"E25.7");var subQ1=sQuery(id+"F0.wireOp",EDGE,"E25.1");var subQ2=sQuery(id+"F0.wireOp",EDGE,"E25.6");var subQ3=sQuery(id+"F0.wireOp",EDGE,"E25.5");var subQ4=sQuery(id+"F0.wireOp",EDGE,"E25.4");var subQ5=sQuery(id+"F0.wireOp",EDGE,"E25.0");var subQ6=sQuery(id+"F0.wireOp",EDGE,"E25.2");var subQ7=sQuery(id+"F0.wireOp",EDGE,"E25.3");Q4=makeQuery(id+"F8.boolean.opBoolean","INTERSECT",EDGE,{"derivedFrom":[makeQuery(id+"F5.boolean.opBoolean","SPLIT",FACE,{"disambiguationData":[TD([makeQuery(id+"F2.opExtrude","SWEPT_FACE",FACE,{"disambiguationData":[OSD([subQ5])]})])],"derivedFrom":makeQuery(id+"F3.boolean.opBoolean","COPY",FACE,{"derivedFrom":makeQuery(id+"F3.opExtrude","CAP_FACE",FACE,{"disambiguationData":[OSD([subQ5,subQ1,subQ6,subQ7,subQ4,subQ3,subQ2,subQ0])],"isStart":false})})}),makeQuery(id+"F8.opExtrude","SWEPT_FACE",FACE,{"disambiguationData":[OSD([sQuery(id+"F7.wireOp",EDGE,"E67")])]})]});}
            var Q5;
            Q5=makeQuery(id+"F8.boolean.opBoolean","INTERSECT",EDGE,{"disambiguationData":[OD(0.0)],"derivedFrom":[makeQuery(id+"F5.opExtrude","SWEPT_FACE",FACE,{"disambiguationData":[OSD([sQuery(id+"F4.wireOp",EDGE,"E30")])]}),makeQuery(id+"F8.opExtrude","SWEPT_FACE",FACE,{"disambiguationData":[OSD([sQuery(id+"F7.wireOp",EDGE,"E67")])]})]});
            fillet(context, id + "F14", {"entities" : qUnion([Q0, Q1, Q2, Q3, Q4, Q5]), "radius" : 3 * mm, "tangentPropagation" : true, "allowEdgeOverflow" : false});
        }
        {
            var Q0;
            Q0=makeQuery(id+"F1.opExtrude","CAP_EDGE",EDGE,{"disambiguationData":[OSD([sQuery(id+"F0.wireOp",EDGE,"E1.bottom")])],"isStart":false});
            fillet(context, id + "F15", {"entities" : qUnion([Q0]), "radius" : 2 * mm, "tangentPropagation" : true, "allowEdgeOverflow" : false});
        }
        {
            var Q0;
            {var subQ0=sQuery(id+"F0.wireOp",EDGE,"E21.filletArc");var subQ1=sQuery(id+"F0.wireOp",EDGE,"E7");var subQ2=sQuery(id+"F0.wireOp",EDGE,"E6");var subQ3=sQuery(id+"F0.wireOp",EDGE,"E5");var subQ4=sQuery(id+"F0.wireOp",EDGE,"E4");var subQ5=sQuery(id+"F0.wireOp",EDGE,"E22.filletArc");var subQ6=sQuery(id+"F0.wireOp",EDGE,"E1.bottom");var subQ7=sQuery(id+"F0.wireOp",EDGE,"E1.right");var subQ8=sQuery(id+"F0.wireOp",EDGE,"E1.top");var subQ9=sQuery(id+"F0.wireOp",EDGE,"E1.left");var subQ10=sQuery(id+"F0.wireOp",EDGE,"E23.filletArc");var subQ11=sQuery(id+"F0.wireOp",EDGE,"E24.filletArc");Q0=makeQuery(id+"F2.boolean.opBoolean","SPLIT",FACE,{"disambiguationData":[TD([makeQuery(id+"F1.opExtrude","SWEPT_FACE",FACE,{"disambiguationData":[OSD([subQ6])]})])],"derivedFrom":makeQuery(id+"F1.opExtrude","CAP_FACE",FACE,{"disambiguationData":[OSD([subQ6,subQ8,subQ9,subQ7,subQ4,subQ3,subQ2,subQ1,subQ0,subQ5,subQ10,subQ11])],"isStart":true})});}
            var sketch = newSketch(context, id + "F16", { "sketchPlane" : qUnion([Q0])});
            skLineSegment(sketch, "E79.1", {"start": v(-70, 90) * mm, "end": v(70, 90) * mm});
            skArc(sketch, "E79.2", {"start": v(-70, 90) * mm, "mid": v(-77.07, 87.07) * mm, "end": v(-80, 80) * mm});
            skLineSegment(sketch, "E79.3", {"start": v(-80, -80) * mm, "end": v(-80, 80) * mm});
            skCircle(sketch, "E79.4", {"center": v(-60, 67.5) * mm, "radius": 4 * mm});
            skCircle(sketch, "E79.5", {"center": v(60, 67.5) * mm, "radius": 4 * mm});
            skArc(sketch, "E79.6", {"start": v(80, 80) * mm, "mid": v(77.07, 87.07) * mm, "end": v(70, 90) * mm});
            skLineSegment(sketch, "E79.7", {"start": v(80, -80) * mm, "end": v(80, 80) * mm});
            skArc(sketch, "E79.8", {"start": v(56.15, 48.18) * mm, "mid": v(0, 67.5) * mm, "end": v(-56.15, 48.18) * mm});
            skArc(sketch, "E79.9", {"start": v(60, 40.3) * mm, "mid": v(58.99, 44.68) * mm, "end": v(56.15, 48.18) * mm});
            skArc(sketch, "E79.10", {"start": v(-56.15, 48.18) * mm, "mid": v(-58.99, 44.68) * mm, "end": v(-60, 40.3) * mm});
            skLineSegment(sketch, "E79.11", {"start": v(-60, 40.3) * mm, "end": v(-60, -40.3) * mm});
            skLineSegment(sketch, "E79.12", {"start": v(60, 40.3) * mm, "end": v(60, -40.3) * mm});
            skArc(sketch, "E79.13", {"start": v(56.15, -48.18) * mm, "mid": v(58.99, -44.68) * mm, "end": v(60, -40.3) * mm});
            skArc(sketch, "E79.14", {"start": v(-56.15, -48.18) * mm, "mid": v(0, -67.5) * mm, "end": v(56.15, -48.18) * mm});
            skArc(sketch, "E79.15", {"start": v(-60, -40.3) * mm, "mid": v(-58.99, -44.68) * mm, "end": v(-56.15, -48.18) * mm});
            skArc(sketch, "E79.16", {"start": v(-80, -80) * mm, "mid": v(-77.07, -87.07) * mm, "end": v(-70, -90) * mm});
            skLineSegment(sketch, "E79.17", {"start": v(-70, -90) * mm, "end": v(70, -90) * mm});
            skCircle(sketch, "E79.18", {"center": v(-60, -67.5) * mm, "radius": 4 * mm});
            skCircle(sketch, "E79.19", {"center": v(60, -67.5) * mm, "radius": 4 * mm});
            skArc(sketch, "E79.20", {"start": v(70, -90) * mm, "mid": v(77.07, -87.07) * mm, "end": v(80, -80) * mm});
            skPoint(sketch, "E79.21", {"position": v(60, 0) * mm});
            skLineSegment(sketch, "E80", {"start": v(0, 90) * mm, "end": v(0, 120) * mm, "construction": true});
            skCircle(sketch, "E81", {"center": v(0, 120) * mm, "radius": 6 * mm});
            skLineSegment(sketch, "E82", {"start": v(-33, 90) * mm, "end": v(-15, 108) * mm});
            skLineSegment(sketch, "E83", {"start": v(-15, 108) * mm, "end": v(-15, 120) * mm});
            skLineSegment(sketch, "E84", {"start": v(33, 90) * mm, "end": v(15, 108) * mm});
            skLineSegment(sketch, "E85", {"start": v(15, 108) * mm, "end": v(15, 120) * mm});
            skArc(sketch, "E86", {"start": v(15, 120) * mm, "mid": v(0, 135) * mm, "end": v(-15, 120) * mm});
            skLineSegment(sketch, "E87", {"start": v(-80, 0) * mm, "end": v(80, 0) * mm, "construction": true});
            skLineSegment(sketch, "E88.MirrorCS", {"start": v(33, -90) * mm, "end": v(15, -108) * mm});
            skLineSegment(sketch, "E89.MirrorCS", {"start": v(15, -108) * mm, "end": v(15, -120) * mm});
            skCircle(sketch, "E90.MirrorC", {"center": v(0, -120) * mm, "radius": 6 * mm});
            skArc(sketch, "E91.MirrorCS", {"start": v(15, -120) * mm, "mid": v(0, -135) * mm, "end": v(-15, -120) * mm});
            skLineSegment(sketch, "E92.MirrorCS", {"start": v(-33, -90) * mm, "end": v(-15, -108) * mm});
            skLineSegment(sketch, "E93.MirrorCS", {"start": v(-15, -108) * mm, "end": v(-15, -120) * mm});
            skLineSegment(sketch, "E94.MirrorCS", {"start": v(0, -90) * mm, "end": v(0, -120) * mm, "construction": true});
            skSolve(sketch);
        }
        {
            var Q0;
            Q0=makeQuery(id+"F16.imprint","IMPRINT",FACE,{"disambiguationData":[TD([[makeQuery(id+"F16.imprint","IMPRINT",EDGE,{"derivedFrom":sQuery(id+"F16.wireOp",EDGE,"E81")}),-1.0]])]});
            var Q1;
            {var subQ5=sQuery(id+"F16.wireOp",EDGE,"E79.2");Q1=makeQuery(id+"F16.imprint","IMPRINT",FACE,{"disambiguationData":[TD([[makeQuery(id+"F16.imprint","IMPRINT",EDGE,{"derivedFrom":subQ5}),1.0]])]});}
            var Q2;
            {var subQ0=sQuery(id+"F16.wireOp",EDGE,"E88.MirrorCS");Q2=makeQuery(id+"F16.imprint","IMPRINT",FACE,{"disambiguationData":[TD([[makeQuery(id+"F16.imprint","IMPRINT",EDGE,{"derivedFrom":subQ0}),-1.0]])]});}
            var Q3;
            Q3=makeQuery(id+"F2.opExtrude","CAP_FACE",FACE,{"disambiguationData":[OSD([sQuery(id+"F0.wireOp",EDGE,"E12"),sQuery(id+"F0.wireOp",EDGE,"E13"),sQuery(id+"F0.wireOp",EDGE,"E14"),sQuery(id+"F0.wireOp",EDGE,"E15"),sQuery(id+"F0.wireOp",EDGE,"E17.filletArc"),sQuery(id+"F0.wireOp",EDGE,"E18.filletArc"),sQuery(id+"F0.wireOp",EDGE,"E19.filletArc"),sQuery(id+"F0.wireOp",EDGE,"E20.filletArc"),sQuery(id+"F0.wireOp",EDGE,"E25.0"),sQuery(id+"F0.wireOp",EDGE,"E25.1"),sQuery(id+"F0.wireOp",EDGE,"E25.2"),sQuery(id+"F0.wireOp",EDGE,"E25.3"),sQuery(id+"F0.wireOp",EDGE,"E25.4"),sQuery(id+"F0.wireOp",EDGE,"E25.5"),sQuery(id+"F0.wireOp",EDGE,"E25.6"),sQuery(id+"F0.wireOp",EDGE,"E25.7")])],"isStart":false});
            extrude(context, id + "F17", {"entities" : qUnion([Q0, Q1, Q2]), "endBound" : BoundingType.UP_TO_SURFACE, "endBoundEntityFace" : qUnion([Q3]), "depth" : 25 * mm});
        }
    });
